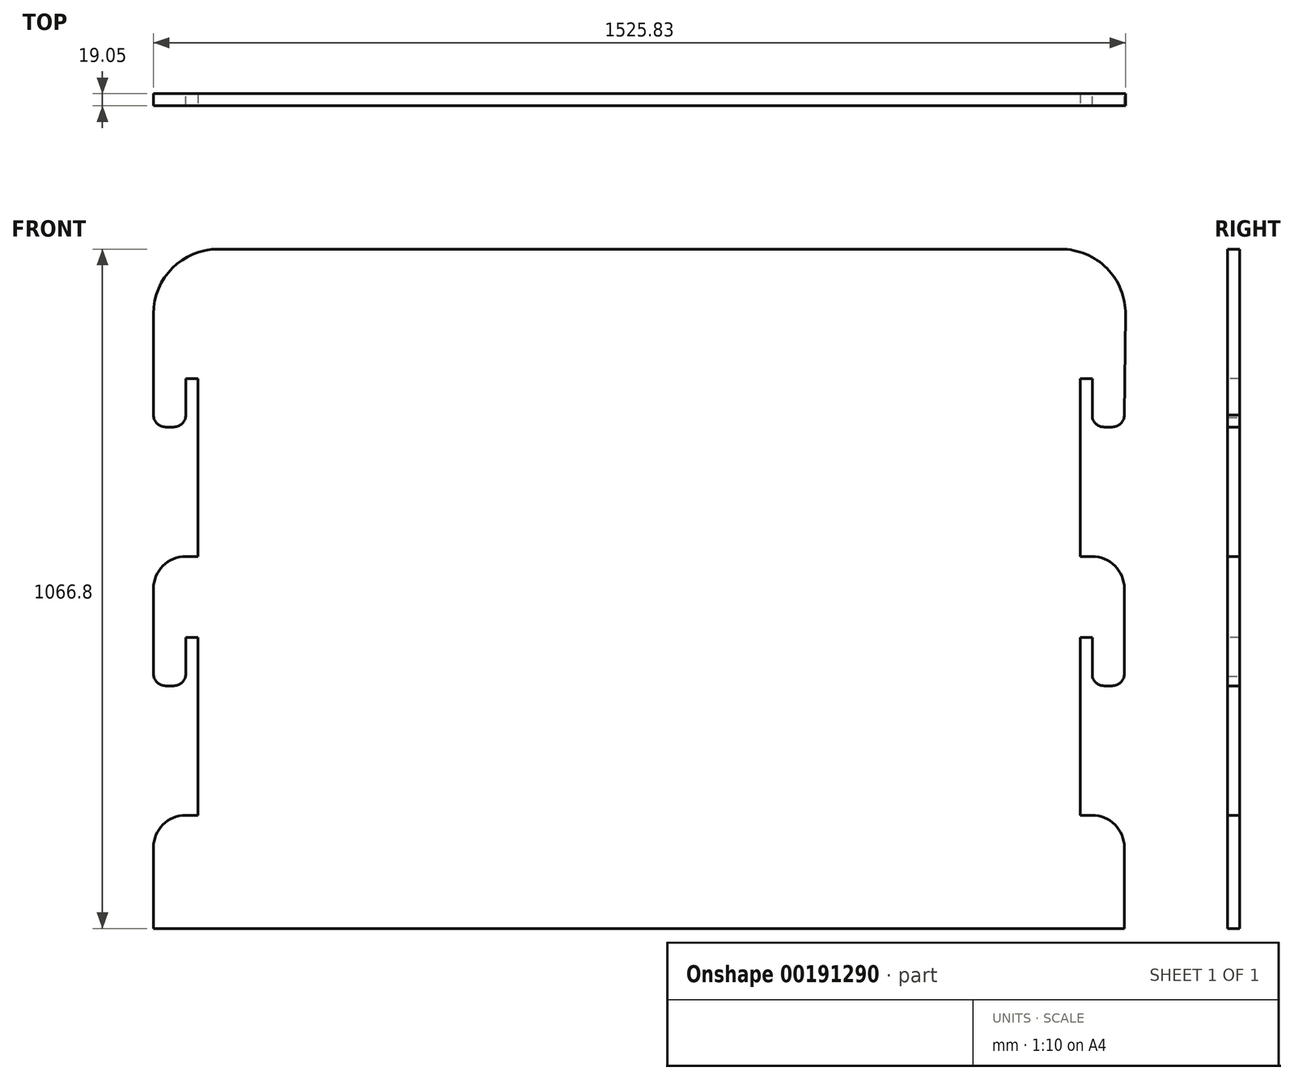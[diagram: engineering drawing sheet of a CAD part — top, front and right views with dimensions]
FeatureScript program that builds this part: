
annotation { "Feature Type Name" : "Feature", "Feature Type Description" : "" }
export const myFeature = defineFeature(function(context is Context, id is Id, definition is map)
    precondition{}
    {
        {
            var Q0;
            Q0=qCreatedBy(makeId("Front.planeOp"),FACE);
            var sketch = newSketch(context, id + "F0", { "sketchPlane" : qUnion([Q0])});
            skArc(sketch, "E0.0", {"start": v(-730.47, 218.49) * mm, "mid": v(-717, 224.07) * mm, "end": v(-711.42, 237.54) * mm});
            skLineSegment(sketch, "E1.0", {"start": v(-743.17, 218.49) * mm, "end": v(-730.47, 218.49) * mm});
            skArc(sketch, "E2.0", {"start": v(-762.22, 237.54) * mm, "mid": v(-756.64, 224.07) * mm, "end": v(-743.17, 218.49) * mm});
            skArc(sketch, "E3.0", {"start": v(-711.42, 15.29) * mm, "mid": v(-747.34, 0.4) * mm, "end": v(-762.22, -35.51) * mm});
            skLineSegment(sketch, "E4.0", {"start": v(-762.22, -35.51) * mm, "end": v(-762.22, -168.86) * mm});
            skArc(sketch, "E5.0", {"start": v(-762.22, -168.86) * mm, "mid": v(-756.64, -182.33) * mm, "end": v(-743.17, -187.91) * mm});
            skLineSegment(sketch, "E6.0", {"start": v(-743.17, -187.91) * mm, "end": v(-730.47, -187.91) * mm});
            skArc(sketch, "E7.0", {"start": v(-730.47, -187.91) * mm, "mid": v(-717, -182.33) * mm, "end": v(-711.42, -168.86) * mm});
            skArc(sketch, "E8.0", {"start": v(-711.42, -391.11) * mm, "mid": v(-747.34, -406) * mm, "end": v(-762.22, -441.91) * mm});
            skLineSegment(sketch, "E9.0", {"start": v(-762.22, -441.91) * mm, "end": v(-762.22, -568.91) * mm});
            skLineSegment(sketch, "E10.0", {"start": v(-762.22, -568.91) * mm, "end": v(-711.42, -568.91) * mm});
            skLineSegment(sketch, "E11.0", {"start": v(-711.42, -568.91) * mm, "end": v(-692.37, -568.91) * mm});
            skLineSegment(sketch, "E12.0", {"start": v(-692.37, -568.91) * mm, "end": v(691.93, -568.91) * mm});
            skLineSegment(sketch, "E13.0", {"start": v(710.98, -568.91) * mm, "end": v(691.93, -568.91) * mm});
            skLineSegment(sketch, "E14.0", {"start": v(710.98, -568.91) * mm, "end": v(761.78, -568.91) * mm});
            skLineSegment(sketch, "E15.0", {"start": v(761.78, -441.91) * mm, "end": v(761.78, -568.91) * mm});
            skArc(sketch, "E16.0", {"start": v(710.98, -391.11) * mm, "mid": v(746.9, -406) * mm, "end": v(761.78, -441.91) * mm});
            skArc(sketch, "E17.0", {"start": v(730.03, -187.91) * mm, "mid": v(716.56, -182.33) * mm, "end": v(710.98, -168.86) * mm});
            skLineSegment(sketch, "E18.0", {"start": v(742.73, -187.91) * mm, "end": v(730.03, -187.91) * mm});
            skArc(sketch, "E19.0", {"start": v(761.78, -168.86) * mm, "mid": v(756.2, -182.33) * mm, "end": v(742.73, -187.91) * mm});
            skLineSegment(sketch, "E20.0", {"start": v(761.78, -35.51) * mm, "end": v(761.78, -168.86) * mm});
            skArc(sketch, "E21.0", {"start": v(710.98, 15.29) * mm, "mid": v(746.9, 0.4) * mm, "end": v(761.78, -35.51) * mm});
            skArc(sketch, "E22.0", {"start": v(730.03, 218.49) * mm, "mid": v(716.56, 224.07) * mm, "end": v(710.98, 237.54) * mm});
            skLineSegment(sketch, "E23.0", {"start": v(742.73, 218.49) * mm, "end": v(730.03, 218.49) * mm});
            skArc(sketch, "E24.0", {"start": v(761.78, 237.54) * mm, "mid": v(756.2, 224.07) * mm, "end": v(742.73, 218.49) * mm});
            skPoint(sketch, "E25.0.start.orphan", {"position": v(761.78, 548.69) * mm});
            skPoint(sketch, "E26.0.start.orphan", {"position": v(-762.22, 548.69) * mm});
            skLineSegment(sketch, "E27", {"start": v(-762.22, 237.54) * mm, "end": v(-762.22, 396.29) * mm});
            skLineSegment(sketch, "E28", {"start": v(-660.62, 497.89) * mm, "end": v(662.01, 497.89) * mm});
            skLineSegment(sketch, "E29", {"start": v(763.6, 395.11) * mm, "end": v(761.78, 237.54) * mm});
            skLineSegment(sketch, "E30", {"start": v(-711.42, 237.54) * mm, "end": v(-711.42, 15.29) * mm});
            skLineSegment(sketch, "E31", {"start": v(-711.42, -168.86) * mm, "end": v(-711.42, -391.11) * mm});
            skLineSegment(sketch, "E32", {"start": v(710.98, -391.11) * mm, "end": v(710.98, -168.86) * mm});
            skLineSegment(sketch, "E33", {"start": v(710.98, 15.29) * mm, "end": v(710.98, 237.54) * mm});
            skPoint(sketch, "E34.visualSharp", {"position": v(-762.22, 497.89) * mm});
            skArc(sketch, "E34.filletArc", {"start": v(-660.62, 497.89) * mm, "mid": v(-732.46, 468.13) * mm, "end": v(-762.22, 396.29) * mm});
            skPoint(sketch, "E35.visualSharp", {"position": v(764.8, 497.89) * mm});
            skArc(sketch, "E35.filletArc", {"start": v(763.6, 395.11) * mm, "mid": v(734.27, 467.71) * mm, "end": v(662.01, 497.89) * mm});
            skLineSegment(sketch, "E36", {"start": v(-0.22, 497.89) * mm, "end": v(0.7, -568.91) * mm, "construction": true});
            skPoint(sketch, "E36.endSnap0", {"position": v(0.7, 497.89) * mm});
            skLineSegment(sketch, "E37", {"start": v(-762.22, 345.49) * mm, "end": v(763.03, 345.49) * mm, "construction": true});
            skSolve(sketch);
        }
        {
            var Q0;
            Q0=makeQuery(id+"F0.imprint","IMPRINT",FACE,{"disambiguationData":[TD([[makeQuery(id+"F0.imprint","IMPRINT",EDGE,{"derivedFrom":sQuery(id+"F0.wireOp",EDGE,"E0.0")}),1.0]])]});
            extrude(context, id + "F1", {"entities" : qUnion([Q0]), "depth" : 19.05 * mm});
        }
        {
            var Q0;
            Q0=makeQuery(id+"F1.opExtrude","CAP_FACE",FACE,{"disambiguationData":[OSD([sQuery(id+"F0.wireOp",EDGE,"E0.0"),sQuery(id+"F0.wireOp",EDGE,"E1.0"),sQuery(id+"F0.wireOp",EDGE,"E2.0"),sQuery(id+"F0.wireOp",EDGE,"E3.0"),sQuery(id+"F0.wireOp",EDGE,"E4.0"),sQuery(id+"F0.wireOp",EDGE,"E5.0"),sQuery(id+"F0.wireOp",EDGE,"E6.0"),sQuery(id+"F0.wireOp",EDGE,"E7.0"),sQuery(id+"F0.wireOp",EDGE,"E8.0"),sQuery(id+"F0.wireOp",EDGE,"E9.0"),sQuery(id+"F0.wireOp",EDGE,"E10.0"),sQuery(id+"F0.wireOp",EDGE,"E11.0"),sQuery(id+"F0.wireOp",EDGE,"E12.0"),sQuery(id+"F0.wireOp",EDGE,"E13.0"),sQuery(id+"F0.wireOp",EDGE,"E14.0"),sQuery(id+"F0.wireOp",EDGE,"E15.0"),sQuery(id+"F0.wireOp",EDGE,"E16.0"),sQuery(id+"F0.wireOp",EDGE,"E17.0"),sQuery(id+"F0.wireOp",EDGE,"E18.0"),sQuery(id+"F0.wireOp",EDGE,"E19.0"),sQuery(id+"F0.wireOp",EDGE,"E20.0"),sQuery(id+"F0.wireOp",EDGE,"E21.0"),sQuery(id+"F0.wireOp",EDGE,"E22.0"),sQuery(id+"F0.wireOp",EDGE,"E23.0"),sQuery(id+"F0.wireOp",EDGE,"E24.0"),sQuery(id+"F0.wireOp",EDGE,"E27"),sQuery(id+"F0.wireOp",EDGE,"E28"),sQuery(id+"F0.wireOp",EDGE,"E29"),sQuery(id+"F0.wireOp",EDGE,"E30"),sQuery(id+"F0.wireOp",EDGE,"E31"),sQuery(id+"F0.wireOp",EDGE,"E32"),sQuery(id+"F0.wireOp",EDGE,"E33"),sQuery(id+"F0.wireOp",EDGE,"E34.filletArc"),sQuery(id+"F0.wireOp",EDGE,"E35.filletArc")])],"isStart":false});
            var sketch = newSketch(context, id + "F2", { "sketchPlane" : qUnion([Q0])});
            skLineSegment(sketch, "E38.bottom", {"start": v(-711.42, 15.29) * mm, "end": v(-692.37, 15.29) * mm});
            skLineSegment(sketch, "E38.top", {"start": v(-711.42, 294.69) * mm, "end": v(-692.37, 294.69) * mm});
            skLineSegment(sketch, "E38.left", {"start": v(-711.42, 15.29) * mm, "end": v(-711.42, 294.69) * mm});
            skLineSegment(sketch, "E38.right", {"start": v(-692.37, 15.29) * mm, "end": v(-692.37, 294.69) * mm});
            skLineSegment(sketch, "E39.bottom", {"start": v(-711.42, -391.11) * mm, "end": v(-692.37, -391.11) * mm});
            skLineSegment(sketch, "E39.top", {"start": v(-711.42, -111.71) * mm, "end": v(-692.37, -111.71) * mm});
            skLineSegment(sketch, "E39.left", {"start": v(-711.42, -391.11) * mm, "end": v(-711.42, -111.71) * mm});
            skLineSegment(sketch, "E39.right", {"start": v(-692.37, -391.11) * mm, "end": v(-692.37, -111.71) * mm});
            skLineSegment(sketch, "E40.MirrorCS", {"start": v(711.42, 294.69) * mm, "end": v(692.37, 294.69) * mm});
            skLineSegment(sketch, "E41.MirrorCS", {"start": v(711.42, 15.29) * mm, "end": v(692.37, 15.29) * mm});
            skLineSegment(sketch, "E42.MirrorCS", {"start": v(711.42, -391.11) * mm, "end": v(692.37, -391.11) * mm});
            skLineSegment(sketch, "E43.MirrorCS", {"start": v(711.42, -111.71) * mm, "end": v(692.37, -111.71) * mm});
            skLineSegment(sketch, "E44.MirrorCS", {"start": v(692.37, -391.11) * mm, "end": v(692.37, -111.71) * mm});
            skLineSegment(sketch, "E45.MirrorCS", {"start": v(711.42, 15.29) * mm, "end": v(711.42, 294.69) * mm});
            skLineSegment(sketch, "E46.MirrorCS", {"start": v(711.42, -391.11) * mm, "end": v(711.42, -111.71) * mm});
            skLineSegment(sketch, "E47.MirrorCS", {"start": v(692.37, 15.29) * mm, "end": v(692.37, 294.69) * mm});
            skSolve(sketch);
        }
        {
            var Q0;
            Q0 = qSketchRegion(id + "F2", true);
            extrude(context, id + "F3", {"entities" : qUnion([Q0]), "operationType" : NewBodyOperationType.REMOVE, "endBound" : BoundingType.THROUGH_ALL, "oppositeDirection" : true, "depth" : 25.4 * mm});
        }
    });
